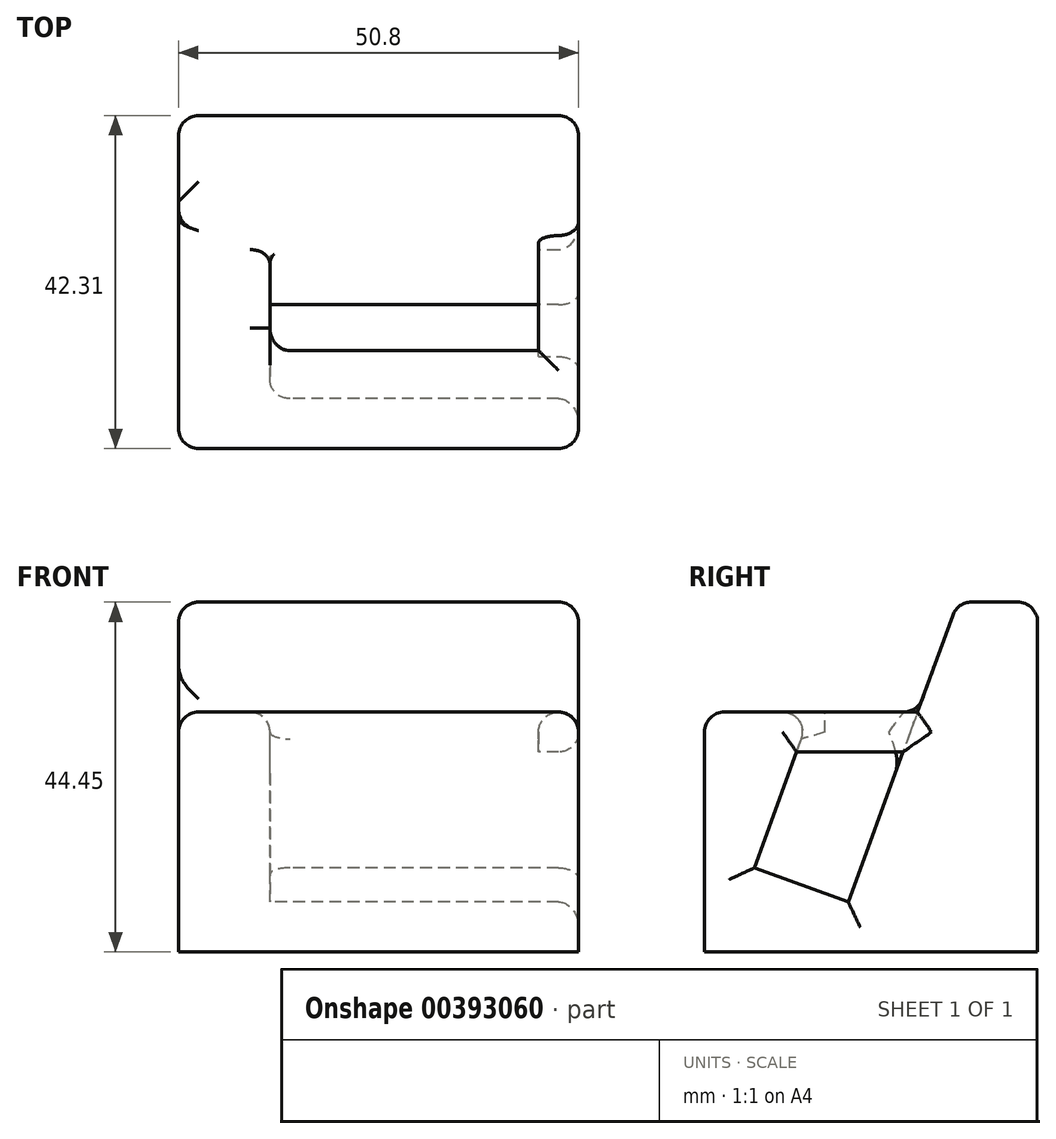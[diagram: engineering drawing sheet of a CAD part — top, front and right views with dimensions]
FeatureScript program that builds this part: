
annotation { "Feature Type Name" : "Feature", "Feature Type Description" : "" }
export const myFeature = defineFeature(function(context is Context, id is Id, definition is map)
    precondition{}
    {
        {
            var Q0;
            Q0=qCreatedBy(makeId("Right.planeOp"),FACE);
            var sketch = newSketch(context, id + "F0", { "sketchPlane" : qUnion([Q0])});
            skLineSegment(sketch, "E0.bottom", {"start": v(0, 0) * mm, "end": v(24.03, 0) * mm});
            skLineSegment(sketch, "E0.top", {"start": v(0, 6.35) * mm, "end": v(24.03, 6.35) * mm});
            skLineSegment(sketch, "E0.left", {"start": v(0, 0) * mm, "end": v(0, 6.35) * mm});
            skLineSegment(sketch, "E0.right", {"start": v(24.03, 0) * mm, "end": v(24.03, 6.35) * mm});
            skLineSegment(sketch, "E1", {"start": v(24.03, 6.35) * mm, "end": v(24.03, 44.45) * mm});
            skLineSegment(sketch, "E2", {"start": v(24.03, 44.45) * mm, "end": v(13.87, 44.45) * mm});
            skLineSegment(sketch, "E3", {"start": v(13.87, 44.45) * mm, "end": v(0, 6.35) * mm});
            skLineSegment(sketch, "E4", {"start": v(0, 6.35) * mm, "end": v(-11.93, 10.7) * mm});
            skLineSegment(sketch, "E5", {"start": v(-11.93, 10.7) * mm, "end": v(-11.93, 0) * mm});
            skLineSegment(sketch, "E6", {"start": v(-11.93, 0) * mm, "end": v(0, 0) * mm});
            skLineSegment(sketch, "E7", {"start": v(-11.93, 10.7) * mm, "end": v(-4.73, 30.48) * mm});
            skLineSegment(sketch, "E8", {"start": v(-4.73, 30.48) * mm, "end": v(-18.28, 30.48) * mm});
            skLineSegment(sketch, "E9", {"start": v(-18.28, 30.48) * mm, "end": v(-18.28, 0) * mm});
            skLineSegment(sketch, "E10", {"start": v(-18.28, 0) * mm, "end": v(-11.93, 0) * mm});
            skSolve(sketch);
        }
        {
            var Q0;
            Q0 = qSketchRegion(id + "F0", true);
            extrude(context, id + "F1", {"entities" : qUnion([Q0]), "endBound" : BoundingType.SYMMETRIC, "depth" : 50.8 * mm});
        }
        {
            var Q0;
            Q0=makeQuery(id+"F1.opExtrude","SWEPT_FACE",FACE,{"disambiguationData":[OSD([sQuery(id+"F0.wireOp",EDGE,"E0.bottom"),sQuery(id+"F0.wireOp",EDGE,"E6"),sQuery(id+"F0.wireOp",EDGE,"E10")])]});
            var sketch = newSketch(context, id + "F2", { "sketchPlane" : qUnion([Q0])});
            skLineSegment(sketch, "E11.bottom", {"start": v(-25.4, -24.03) * mm, "end": v(-13.8, -24.03) * mm});
            skLineSegment(sketch, "E11.top", {"start": v(-25.4, 18.28) * mm, "end": v(-13.8, 18.28) * mm});
            skLineSegment(sketch, "E11.left", {"start": v(-25.4, -24.03) * mm, "end": v(-25.4, 18.28) * mm});
            skLineSegment(sketch, "E11.right", {"start": v(-13.8, -24.03) * mm, "end": v(-13.8, 18.28) * mm});
            skSolve(sketch);
        }
        {
            var Q0;
            Q0 = qSketchRegion(id + "F2", true);
            extrude(context, id + "F3", {"entities" : qUnion([Q0]), "operationType" : NewBodyOperationType.ADD, "oppositeDirection" : true, "depth" : 30.48 * mm});
        }
        {
            var Q0;
            Q0=makeQuery(id+"F1.opExtrude","CAP_FACE",FACE,{"disambiguationData":[OSD([sQuery(id+"F0.wireOp",EDGE,"E0.bottom"),sQuery(id+"F0.wireOp",EDGE,"E0.right"),sQuery(id+"F0.wireOp",EDGE,"E1"),sQuery(id+"F0.wireOp",EDGE,"E2"),sQuery(id+"F0.wireOp",EDGE,"E3"),sQuery(id+"F0.wireOp",EDGE,"E4"),sQuery(id+"F0.wireOp",EDGE,"E6"),sQuery(id+"F0.wireOp",EDGE,"E7"),sQuery(id+"F0.wireOp",EDGE,"E8"),sQuery(id+"F0.wireOp",EDGE,"E9"),sQuery(id+"F0.wireOp",EDGE,"E10")])],"isStart":false});
            var sketch = newSketch(context, id + "F4", { "sketchPlane" : qUnion([Q0])});
            skLineSegment(sketch, "E12.bottom", {"start": v(-18.28, 30.48) * mm, "end": v(24.03, 30.48) * mm});
            skLineSegment(sketch, "E12.top", {"start": v(-18.28, 25.4) * mm, "end": v(24.03, 25.4) * mm});
            skLineSegment(sketch, "E12.left", {"start": v(-18.28, 30.48) * mm, "end": v(-18.28, 25.4) * mm});
            skLineSegment(sketch, "E12.right", {"start": v(24.03, 30.48) * mm, "end": v(24.03, 25.4) * mm});
            skSolve(sketch);
        }
        {
            var Q0;
            Q0 = qSketchRegion(id + "F4", true);
            extrude(context, id + "F5", {"entities" : qUnion([Q0]), "operationType" : NewBodyOperationType.ADD, "oppositeDirection" : true, "depth" : 5.08 * mm});
        }
        {
            var Q0;
            {var subQ1=sQuery(id+"F0.wireOp",EDGE,"E3");var subQ2=sQuery(id+"F0.wireOp",EDGE,"E4");Q0=makeQuery(id+"F5.boolean.opBoolean","SPLIT",EDGE,{"disambiguationData":[TD([makeQuery(id+"F1.opExtrude","SWEPT_FACE",FACE,{"disambiguationData":[OSD([subQ2])]})])],"derivedFrom":makeQuery(id+"F1.opExtrude","CAP_EDGE",EDGE,{"disambiguationData":[OSD([subQ1])],"isStart":false})});}
            var Q1;
            Q1=makeQuery(id+"F5.opExtrude","CAP_EDGE",EDGE,{"disambiguationData":[OSD([sQuery(id+"F4.wireOp",EDGE,"E12.top")])],"isStart":true});
            var Q2;
            Q2=makeQuery(id+"F1.opExtrude","CAP_EDGE",EDGE,{"disambiguationData":[OSD([sQuery(id+"F0.wireOp",EDGE,"E7")])],"isStart":false});
            var Q3;
            Q3=makeQuery(id+"F1.opExtrude","CAP_EDGE",EDGE,{"disambiguationData":[OSD([sQuery(id+"F0.wireOp",EDGE,"E4")])],"isStart":false});
            var Q4;
            Q4=makeQuery(id+"F5.boolean.opBoolean","MERGE",EDGE,{"derivedFrom":[makeQuery(id+"F1.opExtrude","CAP_EDGE",EDGE,{"disambiguationData":[OSD([sQuery(id+"F0.wireOp",EDGE,"E8")])],"isStart":false}),makeQuery(id+"F5.opExtrude","CAP_EDGE",EDGE,{"disambiguationData":[OSD([sQuery(id+"F4.wireOp",EDGE,"E12.bottom")])],"isStart":true})]});
            var Q5;
            Q5=makeQuery(id+"F5.opExtrude","CAP_EDGE",EDGE,{"disambiguationData":[OSD([sQuery(id+"F4.wireOp",EDGE,"E12.bottom")])],"isStart":false});
            var Q6;
            Q6=makeQuery(id+"F1.opExtrude","SWEPT_EDGE",EDGE,{"disambiguationData":[OSD([sQuery(id+"F0.wireOp",EDGE,"E7"),sQuery(id+"F0.wireOp",EDGE,"E8")])]});
            var Q7;
            Q7=makeQuery(id+"F3.opExtrude","CAP_EDGE",EDGE,{"disambiguationData":[OSD([sQuery(id+"F2.wireOp",EDGE,"E11.right")])],"isStart":false});
            var Q8;
            Q8=makeQuery(id+"F1.opExtrude","SWEPT_EDGE",EDGE,{"disambiguationData":[OSD([sQuery(id+"F0.wireOp",EDGE,"E8"),sQuery(id+"F0.wireOp",EDGE,"E9")])]});
            var Q9;
            Q9=makeQuery(id+"F3.boolean.opBoolean","MERGE",EDGE,{"derivedFrom":[makeQuery(id+"F1.opExtrude","CAP_EDGE",EDGE,{"disambiguationData":[OSD([sQuery(id+"F0.wireOp",EDGE,"E8")])],"isStart":true}),makeQuery(id+"F3.opExtrude","CAP_EDGE",EDGE,{"disambiguationData":[OSD([sQuery(id+"F2.wireOp",EDGE,"E11.left")])],"isStart":false})]});
            var Q10;
            Q10=makeQuery(id+"F1.opExtrude","CAP_EDGE",EDGE,{"disambiguationData":[OSD([sQuery(id+"F0.wireOp",EDGE,"E2")])],"isStart":false});
            var Q11;
            {var subQ1=sQuery(id+"F0.wireOp",EDGE,"E3");var subQ2=sQuery(id+"F0.wireOp",EDGE,"E2");Q11=makeQuery(id+"F5.boolean.opBoolean","SPLIT",EDGE,{"disambiguationData":[TD([makeQuery(id+"F1.opExtrude","SWEPT_FACE",FACE,{"disambiguationData":[OSD([subQ2])]})])],"derivedFrom":makeQuery(id+"F1.opExtrude","CAP_EDGE",EDGE,{"disambiguationData":[OSD([subQ1])],"isStart":false})});}
            var Q12;
            Q12=makeQuery(id+"F1.opExtrude","SWEPT_EDGE",EDGE,{"disambiguationData":[OSD([sQuery(id+"F0.wireOp",EDGE,"E2"),sQuery(id+"F0.wireOp",EDGE,"E3")])]});
            var Q13;
            Q13=makeQuery(id+"F3.boolean.opBoolean","INTERSECT",EDGE,{"derivedFrom":[makeQuery(id+"F1.opExtrude","SWEPT_FACE",FACE,{"disambiguationData":[OSD([sQuery(id+"F0.wireOp",EDGE,"E3")])]}),makeQuery(id+"F3.opExtrude","CAP_FACE",FACE,{"disambiguationData":[OSD([sQuery(id+"F2.wireOp",EDGE,"E11.bottom"),sQuery(id+"F2.wireOp",EDGE,"E11.top"),sQuery(id+"F2.wireOp",EDGE,"E11.left"),sQuery(id+"F2.wireOp",EDGE,"E11.right")])],"isStart":false})]});
            var Q14;
            Q14=makeQuery(id+"F1.opExtrude","CAP_EDGE",EDGE,{"disambiguationData":[OSD([sQuery(id+"F0.wireOp",EDGE,"E0.right"),sQuery(id+"F0.wireOp",EDGE,"E1")])],"isStart":false});
            var Q15;
            Q15=makeQuery(id+"F1.opExtrude","CAP_EDGE",EDGE,{"disambiguationData":[OSD([sQuery(id+"F0.wireOp",EDGE,"E9")])],"isStart":false});
            var Q16;
            Q16=makeQuery(id+"F1.opExtrude","CAP_EDGE",EDGE,{"disambiguationData":[OSD([sQuery(id+"F0.wireOp",EDGE,"E9")])],"isStart":true});
            var Q17;
            Q17=makeQuery(id+"F1.opExtrude","CAP_EDGE",EDGE,{"disambiguationData":[OSD([sQuery(id+"F0.wireOp",EDGE,"E0.right"),sQuery(id+"F0.wireOp",EDGE,"E1")])],"isStart":true});
            var Q18;
            Q18=makeQuery(id+"F1.opExtrude","CAP_EDGE",EDGE,{"disambiguationData":[OSD([sQuery(id+"F0.wireOp",EDGE,"E2")])],"isStart":true});
            var Q19;
            Q19=makeQuery(id+"F1.opExtrude","SWEPT_EDGE",EDGE,{"disambiguationData":[OSD([sQuery(id+"F0.wireOp",EDGE,"E1"),sQuery(id+"F0.wireOp",EDGE,"E2")])]});
            var Q20;
            Q20=makeQuery(id+"F3.boolean.opBoolean","INTERSECT",EDGE,{"derivedFrom":[makeQuery(id+"F1.opExtrude","SWEPT_FACE",FACE,{"disambiguationData":[OSD([sQuery(id+"F0.wireOp",EDGE,"E7")])]}),makeQuery(id+"F3.opExtrude","SWEPT_FACE",FACE,{"disambiguationData":[OSD([sQuery(id+"F2.wireOp",EDGE,"E11.right")])]})]});
            fillet(context, id + "F6", {"entities" : qUnion([Q0, Q1, Q2, Q3, Q4, Q5, Q6, Q7, Q8, Q9, Q10, Q11, Q12, Q13, Q14, Q15, Q16, Q17, Q18, Q19, Q20]), "radius" : 2.54 * mm, "tangentPropagation" : true, "allowEdgeOverflow" : false});
        }
    });
